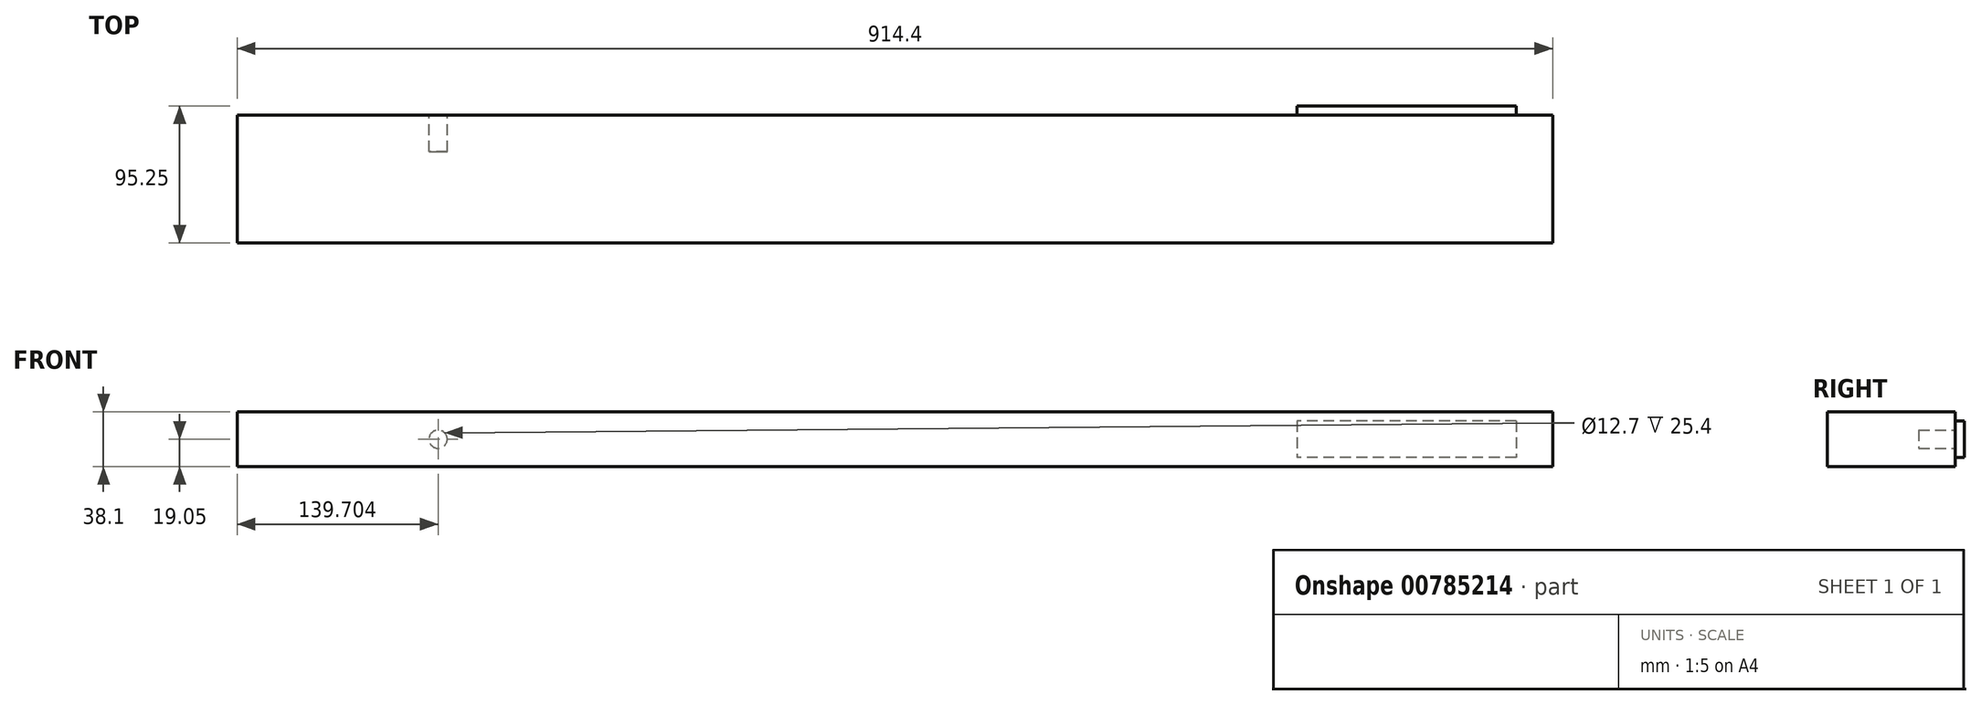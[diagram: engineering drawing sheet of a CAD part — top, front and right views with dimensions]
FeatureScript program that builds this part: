
annotation { "Feature Type Name" : "Feature", "Feature Type Description" : "" }
export const myFeature = defineFeature(function(context is Context, id is Id, definition is map)
    precondition{}
    {
        {
            var Q0;
            Q0=qCreatedBy(makeId("Top.planeOp"),FACE);
            var sketch = newSketch(context, id + "F0", { "sketchPlane" : qUnion([Q0])});
            skLineSegment(sketch, "E0.bottom", {"start": v(-940.53, 31) * mm, "end": v(-26.13, 31) * mm});
            skLineSegment(sketch, "E0.top", {"start": v(-940.53, -57.9) * mm, "end": v(-26.13, -57.9) * mm});
            skLineSegment(sketch, "E0.left", {"start": v(-940.53, 31) * mm, "end": v(-940.53, -57.9) * mm});
            skLineSegment(sketch, "E0.right", {"start": v(-26.13, 31) * mm, "end": v(-26.13, -57.9) * mm});
            skSolve(sketch);
        }
        {
            var Q0;
            Q0=makeQuery(id+"F0.imprint","IMPRINT",FACE,{"disambiguationData":[TD([[makeQuery(id+"F0.imprint","IMPRINT",EDGE,{"derivedFrom":sQuery(id+"F0.wireOp",EDGE,"E0.bottom")}),-1.0]])]});
            extrude(context, id + "F1", {"entities" : qUnion([Q0]), "depth" : 38.1 * mm, "offsetDistance" : 25.4 * mm});
        }
        {
            var Q0;
            Q0=makeQuery(id+"F1.opExtrude","SWEPT_FACE",FACE,{"disambiguationData":[OSD([sQuery(id+"F0.wireOp",EDGE,"E0.bottom")])]});
            var sketch = newSketch(context, id + "F2", { "sketchPlane" : qUnion([Q0])});
            skLineSegment(sketch, "E1.bottom", {"start": v(51.53, 31.75) * mm, "end": v(203.93, 31.75) * mm});
            skLineSegment(sketch, "E1.top", {"start": v(51.53, 6.35) * mm, "end": v(203.93, 6.35) * mm});
            skLineSegment(sketch, "E1.left", {"start": v(51.53, 31.75) * mm, "end": v(51.53, 6.35) * mm});
            skLineSegment(sketch, "E1.right", {"start": v(203.93, 31.75) * mm, "end": v(203.93, 6.35) * mm});
            skSolve(sketch);
        }
        {
            var Q0;
            Q0=makeQuery(id+"F2.imprint","IMPRINT",FACE,{"disambiguationData":[TD([[makeQuery(id+"F2.imprint","IMPRINT",EDGE,{"derivedFrom":sQuery(id+"F2.wireOp",EDGE,"E1.bottom")}),-1.0]])]});
            extrude(context, id + "F3", {"entities" : qUnion([Q0]), "operationType" : NewBodyOperationType.ADD, "depth" : 6.35 * mm, "offsetDistance" : 25.4 * mm});
        }
        {
            var Q0;
            Q0=makeQuery(id+"F1.opExtrude","SWEPT_FACE",FACE,{"disambiguationData":[OSD([sQuery(id+"F0.wireOp",EDGE,"E0.bottom")])]});
            var sketch = newSketch(context, id + "F4", { "sketchPlane" : qUnion([Q0])});
            skCircle(sketch, "E2", {"center": v(800.83, 19.05) * mm, "radius": 6.35 * mm});
            skSolve(sketch);
        }
        {
            var Q0;
            Q0=makeQuery(id+"F4.imprint","IMPRINT",FACE,{"disambiguationData":[TD([[makeQuery(id+"F4.imprint","IMPRINT",EDGE,{"derivedFrom":sQuery(id+"F4.wireOp",EDGE,"E2")}),1.0]])]});
            extrude(context, id + "F5", {"entities" : qUnion([Q0]), "operationType" : NewBodyOperationType.REMOVE, "oppositeDirection" : true, "depth" : 25.4 * mm, "offsetDistance" : 25.4 * mm});
        }
    });
